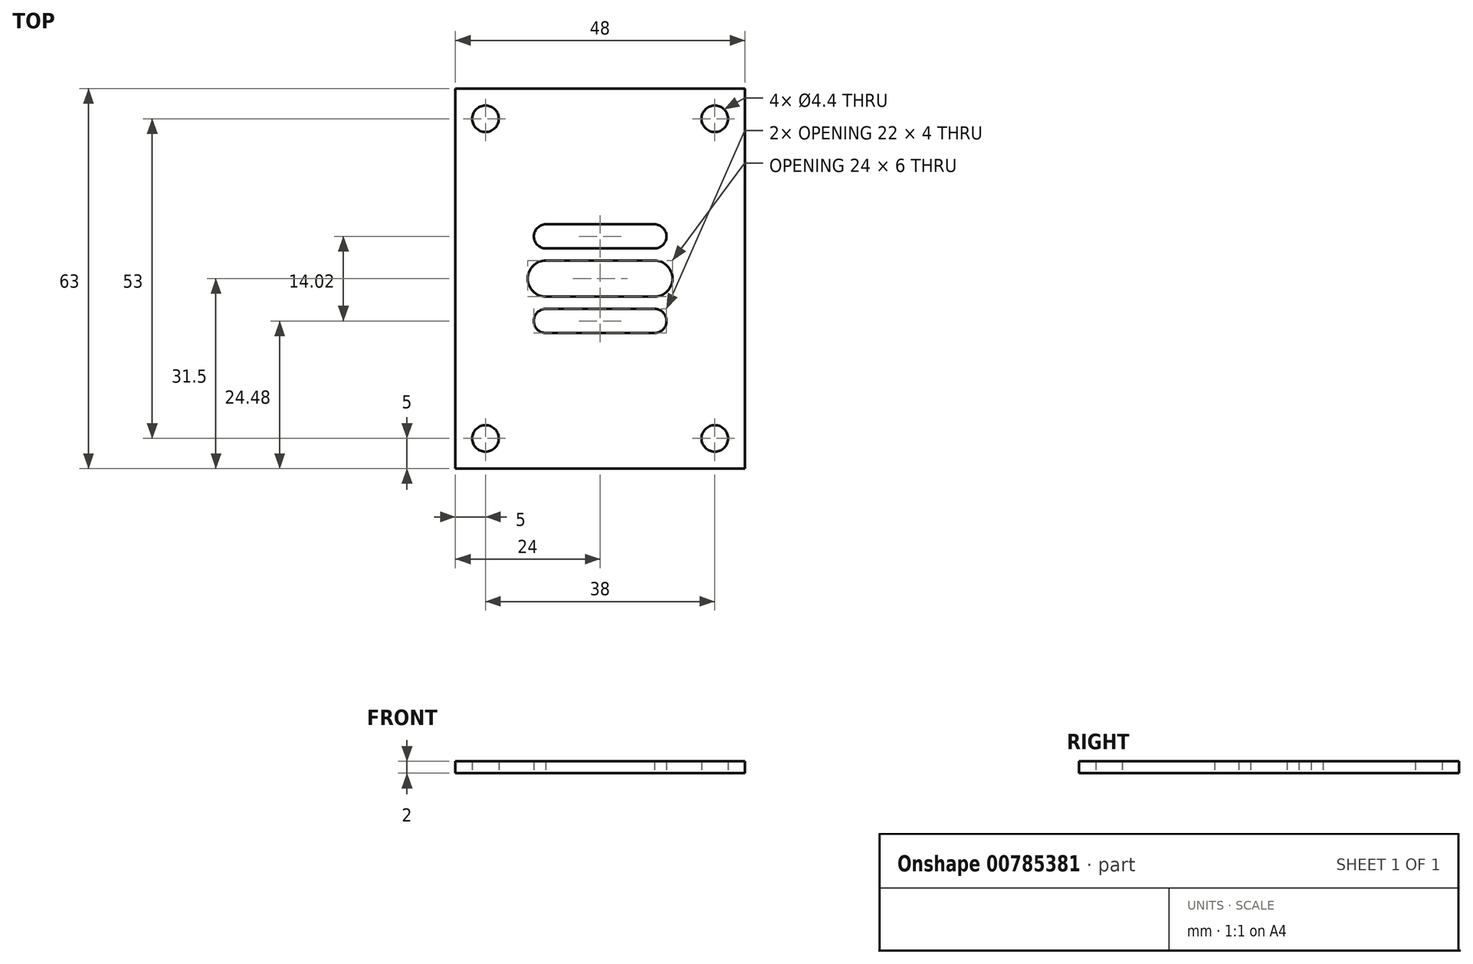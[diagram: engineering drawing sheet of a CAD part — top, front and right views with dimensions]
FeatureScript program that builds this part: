
annotation { "Feature Type Name" : "Feature", "Feature Type Description" : "" }
export const myFeature = defineFeature(function(context is Context, id is Id, definition is map)
    precondition{}
    {
        {
            var Q0;
            Q0=qCreatedBy(makeId("Top.planeOp"),FACE);
            var sketch = newSketch(context, id + "F0", { "sketchPlane" : qUnion([Q0])});
            skLineSegment(sketch, "E0.bottom", {"start": v(0, 0) * mm, "end": v(48, 0) * mm});
            skLineSegment(sketch, "E0.top", {"start": v(0, -63) * mm, "end": v(48, -63) * mm});
            skLineSegment(sketch, "E0.left", {"start": v(0, 0) * mm, "end": v(0, -63) * mm});
            skLineSegment(sketch, "E0.right", {"start": v(48, 0) * mm, "end": v(48, -63) * mm});
            skLineSegment(sketch, "E1", {"start": v(0, -31.5) * mm, "end": v(48, -31.5) * mm});
            skLineSegment(sketch, "E2", {"start": v(24, 0) * mm, "end": v(24, -63) * mm});
            skLineSegment(sketch, "E3.bottom", {"start": v(33, -28.5) * mm, "end": v(15, -28.5) * mm});
            skLineSegment(sketch, "E3.top", {"start": v(33, -34.5) * mm, "end": v(15, -34.5) * mm});
            skLineSegment(sketch, "E3.left", {"start": v(36, -31.5) * mm, "end": v(36, -31.5) * mm});
            skLineSegment(sketch, "E3.right", {"start": v(12, -31.5) * mm, "end": v(12, -31.5) * mm});
            skPoint(sketch, "E3.middle", {"position": v(24, -31.5) * mm});
            skPoint(sketch, "E4.visualSharp", {"position": v(12, -28.5) * mm});
            skArc(sketch, "E4.filletArc", {"start": v(15, -28.5) * mm, "mid": v(12.88, -29.38) * mm, "end": v(12, -31.5) * mm});
            skPoint(sketch, "E5.visualSharp", {"position": v(12, -34.5) * mm});
            skArc(sketch, "E5.filletArc", {"start": v(12, -31.5) * mm, "mid": v(12.88, -33.62) * mm, "end": v(15, -34.5) * mm});
            skPoint(sketch, "E6.visualSharp", {"position": v(36, -28.5) * mm});
            skArc(sketch, "E6.filletArc", {"start": v(36, -31.5) * mm, "mid": v(35.12, -29.38) * mm, "end": v(33, -28.5) * mm});
            skPoint(sketch, "E7.visualSharp", {"position": v(36, -34.5) * mm});
            skArc(sketch, "E7.filletArc", {"start": v(33, -34.5) * mm, "mid": v(35.12, -33.62) * mm, "end": v(36, -31.5) * mm});
            skLineSegment(sketch, "E8.bottom", {"start": v(15, -40.52) * mm, "end": v(33, -40.52) * mm});
            skLineSegment(sketch, "E8.top", {"start": v(15, -36.52) * mm, "end": v(33, -36.52) * mm});
            skLineSegment(sketch, "E8.left", {"start": v(13, -38.52) * mm, "end": v(13, -38.52) * mm});
            skLineSegment(sketch, "E8.right", {"start": v(35, -38.52) * mm, "end": v(35, -38.52) * mm});
            skPoint(sketch, "E8.middle", {"position": v(24, -38.52) * mm});
            skPoint(sketch, "E9.visualSharp", {"position": v(13, -36.52) * mm});
            skArc(sketch, "E9.filletArc", {"start": v(15, -36.52) * mm, "mid": v(13.59, -37.1) * mm, "end": v(13, -38.52) * mm});
            skPoint(sketch, "E10.visualSharp", {"position": v(13, -40.52) * mm});
            skArc(sketch, "E10.filletArc", {"start": v(13, -38.52) * mm, "mid": v(13.59, -39.94) * mm, "end": v(15, -40.52) * mm});
            skPoint(sketch, "E11.visualSharp", {"position": v(35, -40.52) * mm});
            skArc(sketch, "E11.filletArc", {"start": v(33, -40.52) * mm, "mid": v(34.41, -39.94) * mm, "end": v(35, -38.52) * mm});
            skPoint(sketch, "E12.visualSharp", {"position": v(35, -36.52) * mm});
            skArc(sketch, "E12.filletArc", {"start": v(35, -38.52) * mm, "mid": v(34.41, -37.1) * mm, "end": v(33, -36.52) * mm});
            skLineSegment(sketch, "E13.bottom", {"start": v(33, -26.5) * mm, "end": v(15, -26.5) * mm});
            skLineSegment(sketch, "E13.top", {"start": v(33, -22.5) * mm, "end": v(15, -22.5) * mm});
            skLineSegment(sketch, "E13.left", {"start": v(35, -24.5) * mm, "end": v(35, -24.5) * mm});
            skLineSegment(sketch, "E13.right", {"start": v(13, -24.5) * mm, "end": v(13, -24.5) * mm});
            skPoint(sketch, "E13.middle", {"position": v(24, -24.5) * mm});
            skPoint(sketch, "E14.visualSharp", {"position": v(13, -22.5) * mm});
            skArc(sketch, "E14.filletArc", {"start": v(15, -22.5) * mm, "mid": v(13.59, -23.1) * mm, "end": v(13, -24.5) * mm});
            skPoint(sketch, "E15.visualSharp", {"position": v(13, -26.5) * mm});
            skArc(sketch, "E15.filletArc", {"start": v(13, -24.5) * mm, "mid": v(13.59, -25.9) * mm, "end": v(15, -26.5) * mm});
            skPoint(sketch, "E16.visualSharp", {"position": v(35, -22.5) * mm});
            skArc(sketch, "E16.filletArc", {"start": v(35, -24.5) * mm, "mid": v(34.41, -23.1) * mm, "end": v(33, -22.5) * mm});
            skPoint(sketch, "E17.visualSharp", {"position": v(35, -26.5) * mm});
            skArc(sketch, "E17.filletArc", {"start": v(33, -26.5) * mm, "mid": v(34.41, -25.9) * mm, "end": v(35, -24.5) * mm});
            skLineSegment(sketch, "E18.bottom", {"start": v(5, -5) * mm, "end": v(43, -5) * mm, "construction": true});
            skLineSegment(sketch, "E18.top", {"start": v(5, -58) * mm, "end": v(43, -58) * mm, "construction": true});
            skLineSegment(sketch, "E18.left", {"start": v(5, -5) * mm, "end": v(5, -58) * mm, "construction": true});
            skLineSegment(sketch, "E18.right", {"start": v(43, -5) * mm, "end": v(43, -58) * mm, "construction": true});
            skSolve(sketch);
        }
        {
            var Q0;
            Q0=qSketchRegion(id+"F0",true);
            extrude(context, id + "F1", {"entities" : qUnion([Q0]), "depth" : 2 * mm});
        }
        {
            var Q0;
            Q0=sQuery(id+"F0.wireOp",VERTEX,"E18.left.start");
            var Q1;
            Q1=sQuery(id+"F0.wireOp",VERTEX,"E18.bottom.end");
            var Q2;
            Q2=sQuery(id+"F0.wireOp",VERTEX,"E18.top.end");
            var Q3;
            Q3=sQuery(id+"F0.wireOp",VERTEX,"E18.left.end");
            var Q4;
            Q4=makeQuery(id+"F1.opExtrude","SWEPT_BODY",BODY,{"disambiguationData":[OSD([sQuery(id+"F0.wireOp",EDGE,"E0.bottom"),sQuery(id+"F0.wireOp",EDGE,"E0.top"),sQuery(id+"F0.wireOp",EDGE,"E0.left"),sQuery(id+"F0.wireOp",EDGE,"E0.right"),sQuery(id+"F0.wireOp",EDGE,"E3.bottom"),sQuery(id+"F0.wireOp",EDGE,"E3.top"),sQuery(id+"F0.wireOp",EDGE,"E4.filletArc"),sQuery(id+"F0.wireOp",EDGE,"E5.filletArc"),sQuery(id+"F0.wireOp",EDGE,"E6.filletArc"),sQuery(id+"F0.wireOp",EDGE,"E7.filletArc"),sQuery(id+"F0.wireOp",EDGE,"E8.bottom"),sQuery(id+"F0.wireOp",EDGE,"E8.top"),sQuery(id+"F0.wireOp",EDGE,"E9.filletArc"),sQuery(id+"F0.wireOp",EDGE,"E10.filletArc"),sQuery(id+"F0.wireOp",EDGE,"E11.filletArc"),sQuery(id+"F0.wireOp",EDGE,"E12.filletArc"),sQuery(id+"F0.wireOp",EDGE,"E13.bottom"),sQuery(id+"F0.wireOp",EDGE,"E13.top"),sQuery(id+"F0.wireOp",EDGE,"E13.left"),sQuery(id+"F0.wireOp",EDGE,"E13.right"),sQuery(id+"F0.wireOp",EDGE,"E14.filletArc"),sQuery(id+"F0.wireOp",EDGE,"E15.filletArc"),sQuery(id+"F0.wireOp",EDGE,"E16.filletArc"),sQuery(id+"F0.wireOp",EDGE,"E17.filletArc")])]});
            hole(context, id + "F2", {"style" : HoleStyle.SIMPLE, "endStyle" : HoleEndStyle.BLIND, "oppositeDirection" : true, "standardTappedOrClearance" : lookupTablePath({ "standard" : "ISO", "fit" : "Normal", "size" : "M4", "type" : "Clearance" }), "standardBlindInLast" : lookupTablePath({ "fit" : "Standard", "standard" : "ISO", "size" : "M4", "type" : "Clearance" }), "holeDiameter" : 4.4 * mm, "holeDepth" : 5 * mm, "tappedDepth" : 9 * mm, "tapClearance" : 3, "startFromSketch" : true, "locations" : qUnion([Q0, Q1, Q2, Q3]), "scope" : qUnion([Q4])});
        }
    });
